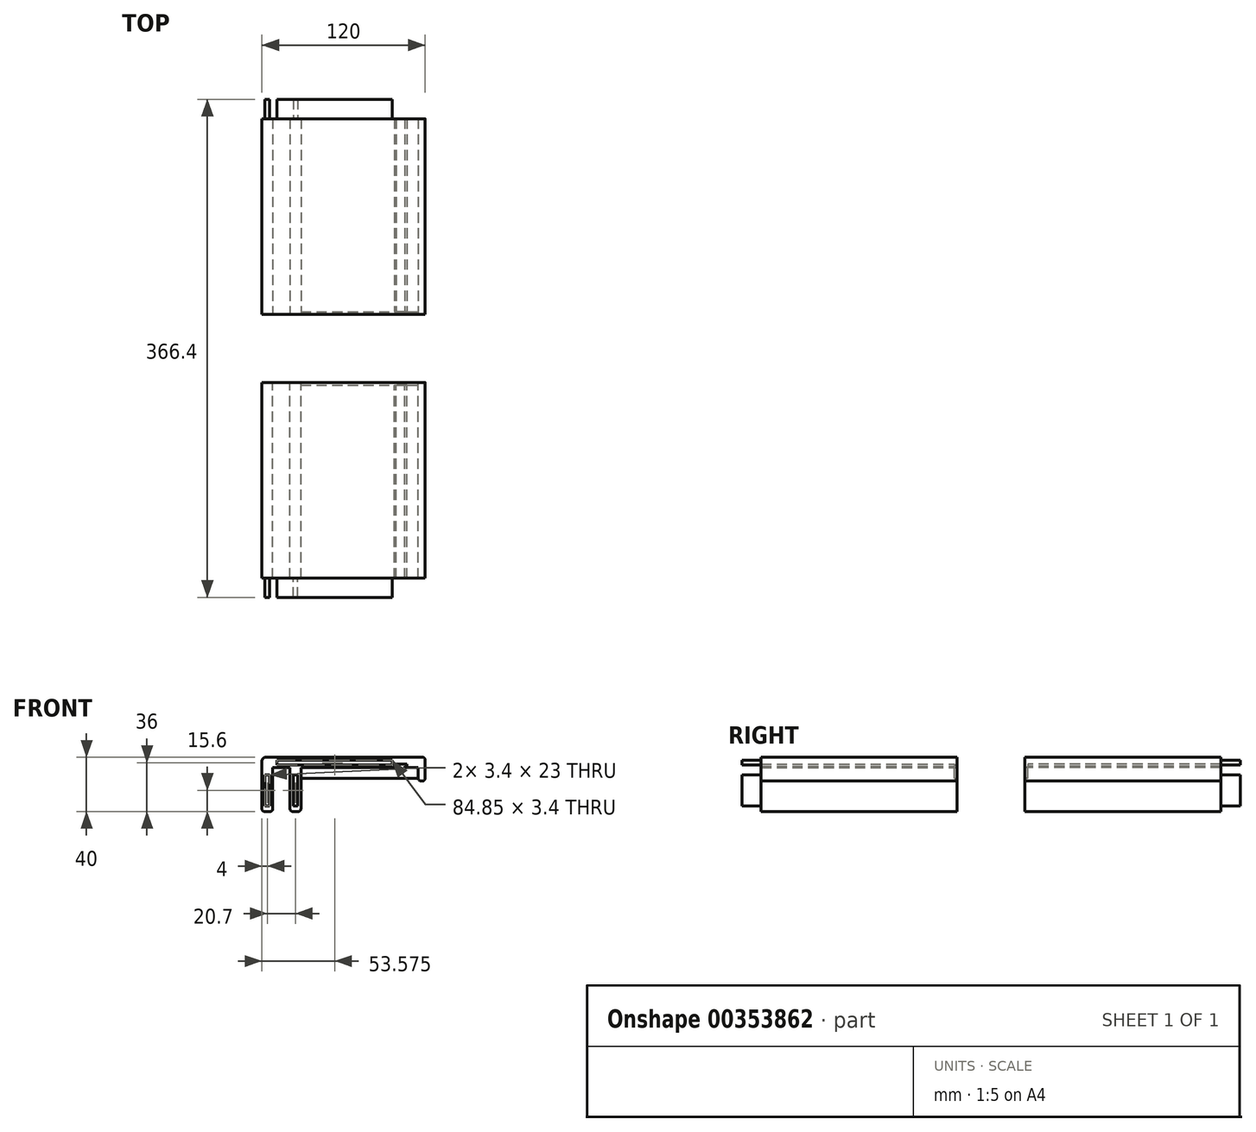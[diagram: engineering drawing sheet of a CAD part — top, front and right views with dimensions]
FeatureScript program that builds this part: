
annotation { "Feature Type Name" : "Feature", "Feature Type Description" : "" }
export const myFeature = defineFeature(function(context is Context, id is Id, definition is map)
    precondition{}
    {
        {
            var Q0;
            Q0=qCreatedBy(makeId("Front.planeOp"),FACE);
            var sketch = newSketch(context, id + "F0", { "sketchPlane" : qUnion([Q0])});
            skLineSegment(sketch, "E0", {"start": v(0, 2) * mm, "end": v(0, 37) * mm});
            skLineSegment(sketch, "E1", {"start": v(3, 40) * mm, "end": v(118, 40) * mm});
            skLineSegment(sketch, "E2", {"start": v(105, 32.4) * mm, "end": v(105, 33.4) * mm});
            skLineSegment(sketch, "E3", {"start": v(105, 33.4) * mm, "end": v(106.75, 33.4) * mm});
            skLineSegment(sketch, "E4", {"start": v(106.75, 33.4) * mm, "end": v(106.75, 34.8) * mm});
            skLineSegment(sketch, "E5", {"start": v(106.75, 34.8) * mm, "end": v(97.45, 34.8) * mm});
            skLineSegment(sketch, "E6", {"start": v(97.45, 34.8) * mm, "end": v(97.45, 33.4) * mm});
            skLineSegment(sketch, "E7", {"start": v(97.45, 33.4) * mm, "end": v(98.7, 33.4) * mm});
            skLineSegment(sketch, "E8", {"start": v(98.7, 33.4) * mm, "end": v(98.7, 32.4) * mm});
            skLineSegment(sketch, "E9", {"start": v(98.7, 32.4) * mm, "end": v(28.7, 32.4) * mm});
            skLineSegment(sketch, "E10", {"start": v(28.7, 32.4) * mm, "end": v(28.7, 2) * mm});
            skLineSegment(sketch, "E11", {"start": v(26.7, 0) * mm, "end": v(22.7, 0) * mm});
            skLineSegment(sketch, "E12", {"start": v(20.7, 2) * mm, "end": v(20.7, 32.4) * mm});
            skLineSegment(sketch, "E13", {"start": v(20.7, 32.4) * mm, "end": v(8, 32.4) * mm});
            skLineSegment(sketch, "E14", {"start": v(8, 32.4) * mm, "end": v(8, 2) * mm});
            skLineSegment(sketch, "E15", {"start": v(6, 0) * mm, "end": v(2, 0) * mm});
            skLineSegment(sketch, "E16", {"start": v(105, 32.4) * mm, "end": v(120, 32.4) * mm});
            skLineSegment(sketch, "E17", {"start": v(120, 38) * mm, "end": v(120, 32.4) * mm});
            skLineSegment(sketch, "E18", {"start": v(120, 32.4) * mm, "end": v(120, 24.4) * mm});
            skLineSegment(sketch, "E19", {"start": v(118, 22.4) * mm, "end": v(117, 22.4) * mm});
            skLineSegment(sketch, "E20", {"start": v(115, 24.4) * mm, "end": v(115, 32.4) * mm});
            skPoint(sketch, "E21.visualSharp", {"position": v(0, 40) * mm});
            skArc(sketch, "E21.filletArc", {"start": v(3, 40) * mm, "mid": v(0.88, 39.12) * mm, "end": v(0, 37) * mm});
            skPoint(sketch, "E22.visualSharp", {"position": v(0, 0) * mm});
            skArc(sketch, "E22.filletArc", {"start": v(0, 2) * mm, "mid": v(0.59, 0.59) * mm, "end": v(2, 0) * mm});
            skPoint(sketch, "E23.visualSharp", {"position": v(8, 0) * mm});
            skArc(sketch, "E23.filletArc", {"start": v(6, 0) * mm, "mid": v(7.41, 0.59) * mm, "end": v(8, 2) * mm});
            skPoint(sketch, "E24.visualSharp", {"position": v(20.7, 0) * mm});
            skArc(sketch, "E24.filletArc", {"start": v(20.7, 2) * mm, "mid": v(21.29, 0.59) * mm, "end": v(22.7, 0) * mm});
            skPoint(sketch, "E25.visualSharp", {"position": v(28.7, 0) * mm});
            skArc(sketch, "E25.filletArc", {"start": v(26.7, 0) * mm, "mid": v(28.11, 0.59) * mm, "end": v(28.7, 2) * mm});
            skPoint(sketch, "E26.visualSharp", {"position": v(120, 22.4) * mm});
            skArc(sketch, "E26.filletArc", {"start": v(118, 22.4) * mm, "mid": v(119.41, 23) * mm, "end": v(120, 24.4) * mm});
            skPoint(sketch, "E27.visualSharp", {"position": v(115, 22.4) * mm});
            skArc(sketch, "E27.filletArc", {"start": v(115, 24.4) * mm, "mid": v(115.59, 23) * mm, "end": v(117, 22.4) * mm});
            skPoint(sketch, "E28.visualSharp", {"position": v(120, 40) * mm});
            skArc(sketch, "E28.filletArc", {"start": v(120, 38) * mm, "mid": v(119.41, 39.41) * mm, "end": v(118, 40) * mm});
            skSolve(sketch);
        }
        {
            var Q0;
            Q0=makeQuery(id+"F0.imprint","IMPRINT",FACE,{"disambiguationData":[TD([[makeQuery(id+"F0.imprint","IMPRINT",EDGE,{"derivedFrom":sQuery(id+"F0.wireOp",EDGE,"E0")}),-1.0]])]});
            var Q1;
            {var subQ1=sQuery(id+"F0.wireOp",EDGE,"E18");Q1=makeQuery(id+"F0.imprint","IMPRINT",FACE,{"disambiguationData":[TD([[makeQuery(id+"F0.imprint","IMPRINT",EDGE,{"derivedFrom":subQ1}),-1.0]])]});}
            extrude(context, id + "F1", {"entities" : qUnion([Q0, Q1]), "depth" : 144 * mm});
        }
        {
            var Q0;
            Q0=makeQuery(id+"F1.opExtrude","CAP_FACE",FACE,{"disambiguationData":[OSD([sQuery(id+"F0.wireOp",EDGE,"E0"),sQuery(id+"F0.wireOp",EDGE,"E1"),sQuery(id+"F0.wireOp",EDGE,"E2"),sQuery(id+"F0.wireOp",EDGE,"E3"),sQuery(id+"F0.wireOp",EDGE,"E4"),sQuery(id+"F0.wireOp",EDGE,"E5"),sQuery(id+"F0.wireOp",EDGE,"E6"),sQuery(id+"F0.wireOp",EDGE,"E7"),sQuery(id+"F0.wireOp",EDGE,"E8"),sQuery(id+"F0.wireOp",EDGE,"E9"),sQuery(id+"F0.wireOp",EDGE,"E10"),sQuery(id+"F0.wireOp",EDGE,"E11"),sQuery(id+"F0.wireOp",EDGE,"E12"),sQuery(id+"F0.wireOp",EDGE,"E13"),sQuery(id+"F0.wireOp",EDGE,"E14"),sQuery(id+"F0.wireOp",EDGE,"E15"),sQuery(id+"F0.wireOp",EDGE,"E16"),sQuery(id+"F0.wireOp",EDGE,"E17"),sQuery(id+"F0.wireOp",EDGE,"E18"),sQuery(id+"F0.wireOp",EDGE,"E19"),sQuery(id+"F0.wireOp",EDGE,"E20"),sQuery(id+"F0.wireOp",EDGE,"E21.filletArc"),sQuery(id+"F0.wireOp",EDGE,"E22.filletArc"),sQuery(id+"F0.wireOp",EDGE,"E23.filletArc"),sQuery(id+"F0.wireOp",EDGE,"E24.filletArc"),sQuery(id+"F0.wireOp",EDGE,"E25.filletArc"),sQuery(id+"F0.wireOp",EDGE,"E26.filletArc"),sQuery(id+"F0.wireOp",EDGE,"E27.filletArc"),sQuery(id+"F0.wireOp",EDGE,"E28.filletArc")])],"isStart":false});
            var sketch = newSketch(context, id + "F2", { "sketchPlane" : qUnion([Q0])});
            skLineSegment(sketch, "E29.bottom", {"start": v(11.15, 37.7) * mm, "end": v(96, 37.7) * mm});
            skLineSegment(sketch, "E29.top", {"start": v(11.15, 34.3) * mm, "end": v(96, 34.3) * mm});
            skLineSegment(sketch, "E29.left", {"start": v(11.15, 37.7) * mm, "end": v(11.15, 34.3) * mm});
            skLineSegment(sketch, "E29.right", {"start": v(96, 37.7) * mm, "end": v(96, 34.3) * mm});
            skLineSegment(sketch, "E30.bottom", {"start": v(2.3, 27.1) * mm, "end": v(5.7, 27.1) * mm});
            skLineSegment(sketch, "E30.top", {"start": v(2.3, 4.1) * mm, "end": v(5.7, 4.1) * mm});
            skLineSegment(sketch, "E30.left", {"start": v(2.3, 27.1) * mm, "end": v(2.3, 4.1) * mm});
            skLineSegment(sketch, "E30.right", {"start": v(5.7, 27.1) * mm, "end": v(5.7, 4.1) * mm});
            skLineSegment(sketch, "E31.bottom", {"start": v(23, 27.1) * mm, "end": v(26.4, 27.1) * mm});
            skLineSegment(sketch, "E31.top", {"start": v(23, 4.1) * mm, "end": v(26.4, 4.1) * mm});
            skLineSegment(sketch, "E31.left", {"start": v(23, 27.1) * mm, "end": v(23, 4.1) * mm});
            skLineSegment(sketch, "E31.right", {"start": v(26.4, 27.1) * mm, "end": v(26.4, 4.1) * mm});
            skSolve(sketch);
        }
        {
            var Q0;
            Q0=makeQuery(id+"F2.imprint","IMPRINT",FACE,{"disambiguationData":[TD([[makeQuery(id+"F2.imprint","IMPRINT",EDGE,{"derivedFrom":sQuery(id+"F2.wireOp",EDGE,"E29.bottom")}),-1.0]])]});
            var Q1;
            Q1=makeQuery(id+"F2.imprint","IMPRINT",FACE,{"disambiguationData":[TD([[makeQuery(id+"F2.imprint","IMPRINT",EDGE,{"derivedFrom":sQuery(id+"F2.wireOp",EDGE,"E30.bottom")}),-1.0]])]});
            var Q2;
            Q2=makeQuery(id+"F2.imprint","IMPRINT",FACE,{"disambiguationData":[TD([[makeQuery(id+"F2.imprint","IMPRINT",EDGE,{"derivedFrom":sQuery(id+"F2.wireOp",EDGE,"E31.bottom")}),-1.0]])]});
            extrude(context, id + "F3", {"entities" : qUnion([Q0, Q1, Q2]), "operationType" : NewBodyOperationType.ADD, "depth" : 14.2 * mm});
        }
        {
            var Q0;
            Q0=makeQuery(id+"F1.opExtrude","CAP_FACE",FACE,{"disambiguationData":[OSD([sQuery(id+"F0.wireOp",EDGE,"E0"),sQuery(id+"F0.wireOp",EDGE,"E1"),sQuery(id+"F0.wireOp",EDGE,"E2"),sQuery(id+"F0.wireOp",EDGE,"E3"),sQuery(id+"F0.wireOp",EDGE,"E4"),sQuery(id+"F0.wireOp",EDGE,"E5"),sQuery(id+"F0.wireOp",EDGE,"E6"),sQuery(id+"F0.wireOp",EDGE,"E7"),sQuery(id+"F0.wireOp",EDGE,"E8"),sQuery(id+"F0.wireOp",EDGE,"E9"),sQuery(id+"F0.wireOp",EDGE,"E10"),sQuery(id+"F0.wireOp",EDGE,"E11"),sQuery(id+"F0.wireOp",EDGE,"E12"),sQuery(id+"F0.wireOp",EDGE,"E13"),sQuery(id+"F0.wireOp",EDGE,"E14"),sQuery(id+"F0.wireOp",EDGE,"E15"),sQuery(id+"F0.wireOp",EDGE,"E16"),sQuery(id+"F0.wireOp",EDGE,"E17"),sQuery(id+"F0.wireOp",EDGE,"E18"),sQuery(id+"F0.wireOp",EDGE,"E19"),sQuery(id+"F0.wireOp",EDGE,"E20"),sQuery(id+"F0.wireOp",EDGE,"E21.filletArc"),sQuery(id+"F0.wireOp",EDGE,"E22.filletArc"),sQuery(id+"F0.wireOp",EDGE,"E23.filletArc"),sQuery(id+"F0.wireOp",EDGE,"E24.filletArc"),sQuery(id+"F0.wireOp",EDGE,"E25.filletArc"),sQuery(id+"F0.wireOp",EDGE,"E26.filletArc"),sQuery(id+"F0.wireOp",EDGE,"E27.filletArc"),sQuery(id+"F0.wireOp",EDGE,"E28.filletArc")])],"isStart":true});
            var sketch = newSketch(context, id + "F4", { "sketchPlane" : qUnion([Q0])});
            skLineSegment(sketch, "E32", {"start": v(-105, 32.4) * mm, "end": v(-105, 33.4) * mm});
            skLineSegment(sketch, "E33", {"start": v(-105, 33.4) * mm, "end": v(-106.75, 33.4) * mm});
            skLineSegment(sketch, "E34", {"start": v(-106.75, 33.4) * mm, "end": v(-106.75, 34.8) * mm});
            skLineSegment(sketch, "E35", {"start": v(-106.75, 34.8) * mm, "end": v(-97.45, 34.8) * mm});
            skLineSegment(sketch, "E36", {"start": v(-97.45, 34.8) * mm, "end": v(-97.45, 33.4) * mm});
            skLineSegment(sketch, "E37", {"start": v(-97.45, 33.4) * mm, "end": v(-98.7, 33.4) * mm});
            skLineSegment(sketch, "E38", {"start": v(-98.7, 33.4) * mm, "end": v(-98.7, 32.4) * mm});
            skLineSegment(sketch, "E39", {"start": v(-98.7, 32.4) * mm, "end": v(-105, 32.4) * mm});
            skSolve(sketch);
        }
        {
            var Q0;
            Q0=qSketchRegion(id+"F4",true);
            extrude(context, id + "F5", {"entities" : qUnion([Q0]), "operationType" : NewBodyOperationType.ADD, "oppositeDirection" : true, "depth" : 2 * mm});
        }
        {
            var Q0;
            Q0=makeQuery(id+"F5.boolean.opBoolean","MERGE",FACE,{"derivedFrom":[makeQuery(id+"F1.opExtrude","SWEPT_FACE",FACE,{"disambiguationData":[OSD([sQuery(id+"F0.wireOp",EDGE,"E9")])]}),makeQuery(id+"F1.opExtrude","SWEPT_FACE",FACE,{"disambiguationData":[OSD([sQuery(id+"F0.wireOp",EDGE,"E16")])]}),makeQuery(id+"F5.opExtrude","SWEPT_FACE",FACE,{"disambiguationData":[OSD([sQuery(id+"F4.wireOp",EDGE,"E39")])]})]});
            var sketch = newSketch(context, id + "F6", { "sketchPlane" : qUnion([Q0])});
            skLineSegment(sketch, "E40.bottom", {"start": v(115, 0) * mm, "end": v(28.7, 0) * mm});
            skLineSegment(sketch, "E40.top", {"start": v(115, 2) * mm, "end": v(28.7, 2) * mm});
            skLineSegment(sketch, "E40.left", {"start": v(115, 0) * mm, "end": v(115, 2) * mm});
            skLineSegment(sketch, "E40.right", {"start": v(28.7, 0) * mm, "end": v(28.7, 2) * mm});
            skSolve(sketch);
        }
        {
            var Q0;
            Q0=makeQuery(id+"F6.imprint","IMPRINT",FACE,{"disambiguationData":[TD([[makeQuery(id+"F6.imprint","IMPRINT",EDGE,{"derivedFrom":sQuery(id+"F6.wireOp",EDGE,"E40.bottom")}),-1.0]])]});
            var Q1;
            Q1=makeQuery(id+"F1.opExtrude","CAP_VERTEX",VERTEX,{"disambiguationData":[OSD([sQuery(id+"F0.wireOp",EDGE,"E20"),sQuery(id+"F0.wireOp",EDGE,"E27.filletArc")])],"isStart":true});
            extrude(context, id + "F7", {"entities" : qUnion([Q0]), "operationType" : NewBodyOperationType.ADD, "endBound" : BoundingType.UP_TO_VERTEX, "endBoundEntityVertex" : qUnion([Q1]), "depth" : 25 * mm});
        }
        {
            var Q0;
            Q0=qCreatedBy(makeId("Front.planeOp"),FACE);
            cPlane(context, id + "F8", {"entities" : qUnion([Q0]), "cplaneType" : CPlaneType.OFFSET, "offset" : 25 * mm, "oppositeDirection" : true, "width" : 150 * mm, "height" : 150 * mm});
        }
        {
            var Q0;
            Q0=makeQuery(id+"F1.opExtrude","SWEPT_BODY",BODY,{"disambiguationData":[OSD([sQuery(id+"F0.wireOp",EDGE,"E0"),sQuery(id+"F0.wireOp",EDGE,"E1"),sQuery(id+"F0.wireOp",EDGE,"E2"),sQuery(id+"F0.wireOp",EDGE,"E3"),sQuery(id+"F0.wireOp",EDGE,"E4"),sQuery(id+"F0.wireOp",EDGE,"E5"),sQuery(id+"F0.wireOp",EDGE,"E6"),sQuery(id+"F0.wireOp",EDGE,"E7"),sQuery(id+"F0.wireOp",EDGE,"E8"),sQuery(id+"F0.wireOp",EDGE,"E9"),sQuery(id+"F0.wireOp",EDGE,"E10"),sQuery(id+"F0.wireOp",EDGE,"E11"),sQuery(id+"F0.wireOp",EDGE,"E12"),sQuery(id+"F0.wireOp",EDGE,"E13"),sQuery(id+"F0.wireOp",EDGE,"E14"),sQuery(id+"F0.wireOp",EDGE,"E15"),sQuery(id+"F0.wireOp",EDGE,"E16"),sQuery(id+"F0.wireOp",EDGE,"E17"),sQuery(id+"F0.wireOp",EDGE,"E18"),sQuery(id+"F0.wireOp",EDGE,"E19"),sQuery(id+"F0.wireOp",EDGE,"E20"),sQuery(id+"F0.wireOp",EDGE,"E21.filletArc"),sQuery(id+"F0.wireOp",EDGE,"E22.filletArc"),sQuery(id+"F0.wireOp",EDGE,"E23.filletArc"),sQuery(id+"F0.wireOp",EDGE,"E24.filletArc"),sQuery(id+"F0.wireOp",EDGE,"E25.filletArc"),sQuery(id+"F0.wireOp",EDGE,"E26.filletArc"),sQuery(id+"F0.wireOp",EDGE,"E27.filletArc"),sQuery(id+"F0.wireOp",EDGE,"E28.filletArc")])]});
            var Q1;
            Q1=qCreatedBy(id+"F8.planeOp",FACE);
            mirror(context, id + "F9", {"entities" : qUnion([Q0]), "mirrorPlane" : qUnion([Q1])});
        }
    });
